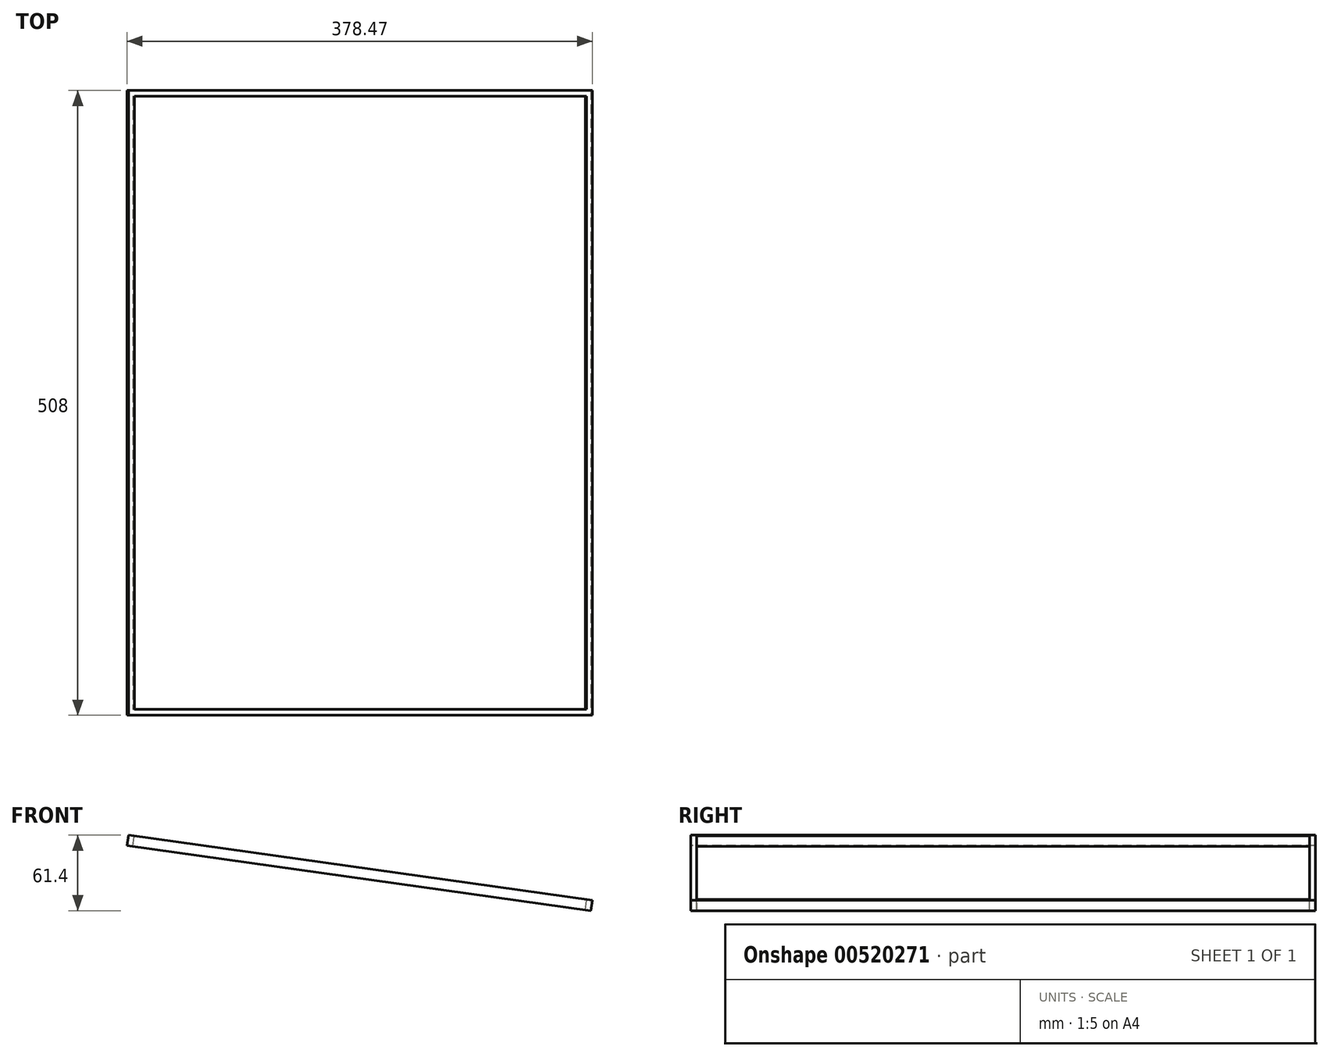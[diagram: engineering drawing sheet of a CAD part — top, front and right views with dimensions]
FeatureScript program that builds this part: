
annotation { "Feature Type Name" : "Feature", "Feature Type Description" : "" }
export const myFeature = defineFeature(function(context is Context, id is Id, definition is map)
    precondition{}
    {
        {
            var Q0;
            Q0=qCreatedBy(makeId("Front.planeOp"),FACE);
            var sketch = newSketch(context, id + "F0", { "sketchPlane" : qUnion([Q0])});
            skLineSegment(sketch, "E0", {"start": v(-177.07, 0) * mm, "end": v(200.48, 0) * mm, "construction": true});
            skLineSegment(sketch, "E1", {"start": v(0, 173.67) * mm, "end": v(0, -174.1) * mm, "construction": true});
            skLineSegment(sketch, "E2", {"start": v(-176.8, 53.02) * mm, "end": v(200.48, 0) * mm});
            skLineSegment(sketch, "E3", {"start": v(-176.8, 53.02) * mm, "end": v(-175.63, 61.4) * mm});
            skLineSegment(sketch, "E4", {"start": v(-175.63, 61.4) * mm, "end": v(201.66, 8.38) * mm});
            skLineSegment(sketch, "E5", {"start": v(201.66, 8.38) * mm, "end": v(200.48, 0) * mm});
            skSolve(sketch);
        }
        {
            var Q0;
            Q0=makeQuery(id+"F0.imprint","IMPRINT",FACE,{"disambiguationData":[TD([[makeQuery(id+"F0.imprint","IMPRINT",EDGE,{"derivedFrom":sQuery(id+"F0.wireOp",EDGE,"E2")}),1.0]])]});
            extrude(context, id + "F1", {"entities" : qUnion([Q0]), "oppositeDirection" : true, "depth" : 508 * mm, "offsetDistance" : 25.4 * mm});
        }
        {
            var Q0;
            Q0=makeQuery(id+"F1.opExtrude","SWEPT_FACE",FACE,{"disambiguationData":[OSD([sQuery(id+"F0.wireOp",EDGE,"E4")])]});
            var sketch = newSketch(context, id + "F2", { "sketchPlane" : qUnion([Q0])});
            skLineSegment(sketch, "E6", {"start": v(-182.47, 254) * mm, "end": v(198.53, 254) * mm, "construction": true});
            skLineSegment(sketch, "E7", {"start": v(0, 0) * mm, "end": v(0, 1141.5) * mm, "construction": true});
            skLineSegment(sketch, "E8", {"start": v(-177.72, 503.25) * mm, "end": v(193.78, 503.25) * mm});
            skLineSegment(sketch, "E9", {"start": v(193.78, 503.25) * mm, "end": v(193.78, 4.75) * mm});
            skLineSegment(sketch, "E10", {"start": v(193.78, 4.75) * mm, "end": v(-177.72, 4.75) * mm});
            skLineSegment(sketch, "E11", {"start": v(-177.72, 4.75) * mm, "end": v(-177.72, 503.25) * mm});
            skSolve(sketch);
        }
        {
            var Q0;
            Q0 = qSketchRegion(id + "F2", true);
            extrude(context, id + "F3", {"entities" : qUnion([Q0]), "operationType" : NewBodyOperationType.REMOVE, "oppositeDirection" : true, "depth" : 25.4 * mm, "offsetDistance" : 25.4 * mm});
        }
    });
